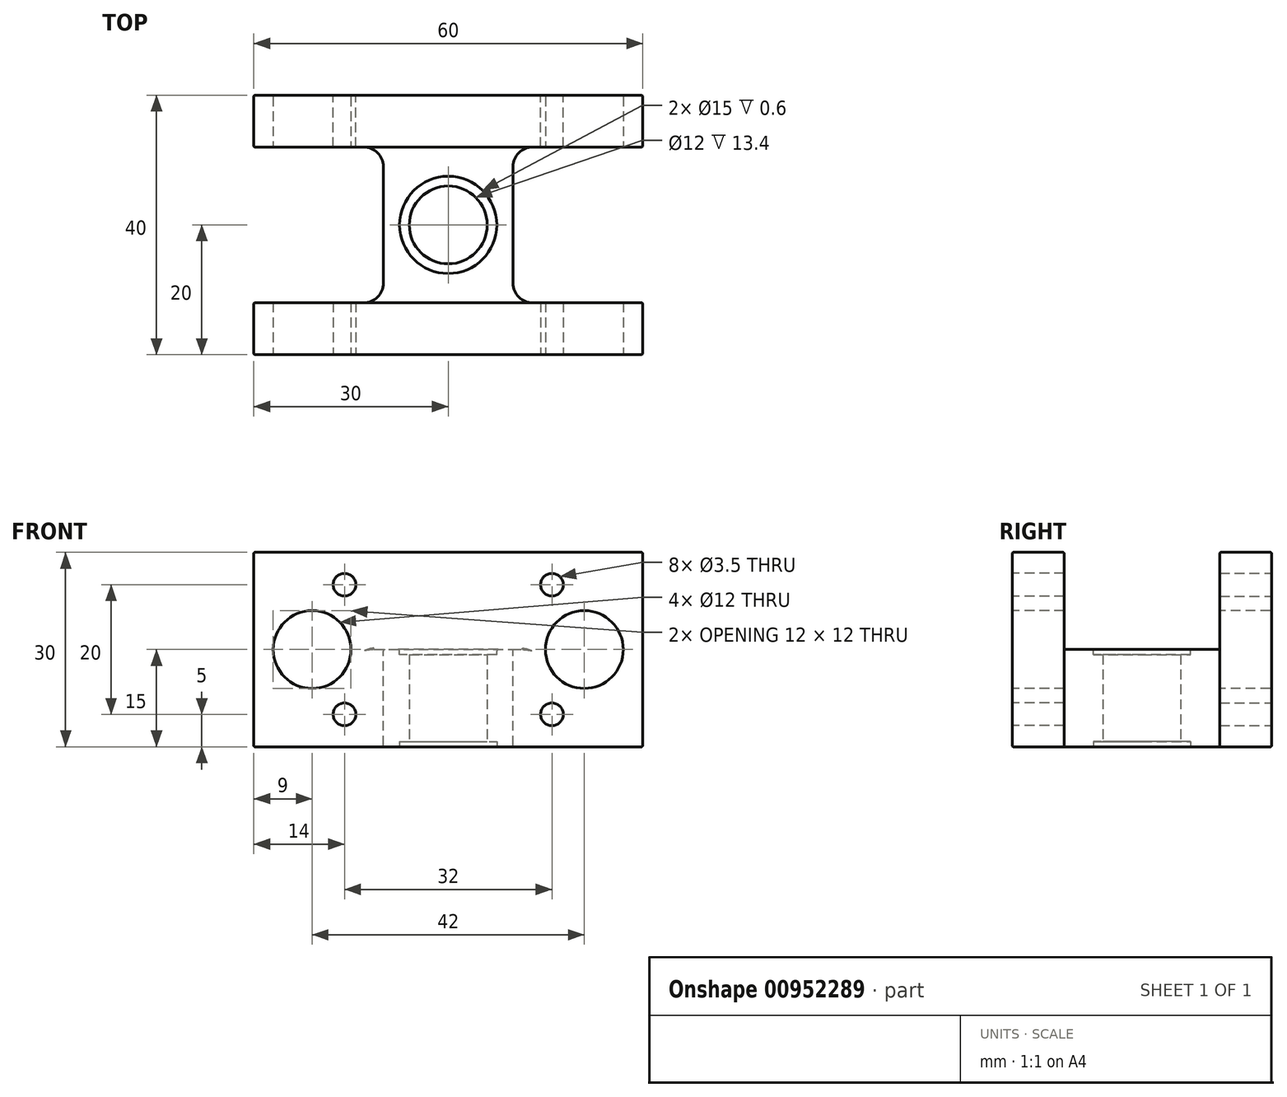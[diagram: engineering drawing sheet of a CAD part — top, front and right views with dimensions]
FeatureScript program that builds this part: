
annotation { "Feature Type Name" : "Feature", "Feature Type Description" : "" }
export const myFeature = defineFeature(function(context is Context, id is Id, definition is map)
    precondition{}
    {
        {
            var Q0;
            Q0=qCreatedBy(makeId("Top.planeOp"),FACE);
            var sketch = newSketch(context, id + "F0", { "sketchPlane" : qUnion([Q0])});
            skLineSegment(sketch, "E0.bottom", {"start": v(30, -20) * mm, "end": v(-30, -20) * mm});
            skLineSegment(sketch, "E0.top", {"start": v(30, 20) * mm, "end": v(-30, 20) * mm});
            skLineSegment(sketch, "E0.left", {"start": v(30, -20) * mm, "end": v(30, 20) * mm});
            skLineSegment(sketch, "E0.right", {"start": v(-30, -20) * mm, "end": v(-30, 20) * mm});
            skPoint(sketch, "E0.middle", {"position": v(0, 0) * mm});
            skCircle(sketch, "E1", {"center": v(0, 0) * mm, "radius": 6 * mm});
            skSolve(sketch);
        }
        {
            var Q0;
            Q0 = qSketchRegion(id + "F0", true);
            extrude(context, id + "F1", {"entities" : qUnion([Q0]), "depth" : 15 * mm, "offsetDistance" : 25 * mm, "symmetric" : true});
        }
        {
            var Q0;
            Q0=makeQuery(id+"F1.opExtrude","SWEPT_FACE",FACE,{"disambiguationData":[OSD([sQuery(id+"F0.wireOp",EDGE,"E0.left")])]});
            var sketch = newSketch(context, id + "F2", { "sketchPlane" : qUnion([Q0])});
            skLineSegment(sketch, "E2.bottom", {"start": v(20, 7.5) * mm, "end": v(12, 7.5) * mm});
            skLineSegment(sketch, "E2.top", {"start": v(20, 22.5) * mm, "end": v(12, 22.5) * mm});
            skLineSegment(sketch, "E2.left", {"start": v(20, 7.5) * mm, "end": v(20, 22.5) * mm});
            skLineSegment(sketch, "E2.right", {"start": v(12, 7.5) * mm, "end": v(12, 22.5) * mm});
            skLineSegment(sketch, "E3.MirrorCS", {"start": v(-12, 7.5) * mm, "end": v(-12, 22.5) * mm});
            skLineSegment(sketch, "E4.MirrorCS", {"start": v(-20, 22.5) * mm, "end": v(-12, 22.5) * mm});
            skLineSegment(sketch, "E5.MirrorCS", {"start": v(-20, 7.5) * mm, "end": v(-20, 22.5) * mm});
            skSolve(sketch);
        }
        {
            var Q0;
            Q0 = qSketchRegion(id + "F2", true);
            var Q1;
            {var subQ0=sQuery(id+"F2.wireOp",EDGE,"E3.MirrorCS");Q1=makeQuery(id+"F2.imprint","IMPRINT",FACE,{"disambiguationData":[TD([[makeQuery(id+"F2.imprint","IMPRINT",EDGE,{"derivedFrom":subQ0}),1.0]])]});}
            var Q2;
            Q2=makeQuery(id+"F1.opExtrude","SWEPT_FACE",FACE,{"disambiguationData":[OSD([sQuery(id+"F0.wireOp",EDGE,"E0.right")])]});
            extrude(context, id + "F3", {"entities" : qUnion([Q0, Q1]), "operationType" : NewBodyOperationType.ADD, "endBound" : BoundingType.UP_TO_SURFACE, "oppositeDirection" : true, "depth" : 25 * mm, "endBoundEntityFace" : qUnion([Q2]), "offsetDistance" : 25 * mm});
        }
        {
            var Q0;
            Q0=makeQuery(id+"F3.boolean.opBoolean","MERGE",FACE,{"derivedFrom":[makeQuery(id+"F1.opExtrude","SWEPT_FACE",FACE,{"disambiguationData":[OSD([sQuery(id+"F0.wireOp",EDGE,"E0.top")])]}),makeQuery(id+"F3.opExtrude","SWEPT_FACE",FACE,{"disambiguationData":[OSD([sQuery(id+"F2.wireOp",EDGE,"E2.left")])]})]});
            var sketch = newSketch(context, id + "F4", { "sketchPlane" : qUnion([Q0])});
            skCircle(sketch, "E6", {"center": v(16, 17.5) * mm, "radius": 1.75 * mm});
            skCircle(sketch, "E7.MirrorC", {"center": v(-16, 17.5) * mm, "radius": 1.75 * mm});
            skLineSegment(sketch, "E8", {"start": v(30, 7.5) * mm, "end": v(17.34, 7.5) * mm});
            skCircle(sketch, "E9.MirrorC", {"center": v(16, -2.5) * mm, "radius": 1.75 * mm});
            skCircle(sketch, "E10.MirrorC", {"center": v(-16, -2.5) * mm, "radius": 1.75 * mm});
            skSolve(sketch);
        }
        {
            var Q0;
            Q0 = qSketchRegion(id + "F4", true);
            var Q1;
            Q1=makeQuery(id+"F3.opExtrude","SWEPT_FACE",FACE,{"disambiguationData":[OSD([sQuery(id+"F2.wireOp",EDGE,"E2.right")])]});
            extrude(context, id + "F5", {"entities" : qUnion([Q0]), "operationType" : NewBodyOperationType.REMOVE, "oppositeDirection" : true, "depth" : 8 * mm, "endBoundEntityFace" : qUnion([Q1]), "offsetDistance" : 25 * mm});
        }
        {
            var Q0;
            Q0=makeQuery(id+"F3.boolean.opBoolean","MERGE",FACE,{"derivedFrom":[makeQuery(id+"F1.opExtrude","SWEPT_FACE",FACE,{"disambiguationData":[OSD([sQuery(id+"F0.wireOp",EDGE,"E0.bottom")])]}),makeQuery(id+"F3.opExtrude","SWEPT_FACE",FACE,{"disambiguationData":[OSD([sQuery(id+"F2.wireOp",EDGE,"E5.MirrorCS")])]})]});
            var sketch = newSketch(context, id + "F6", { "sketchPlane" : qUnion([Q0])});
            skCircle(sketch, "E11", {"center": v(16, 17.5) * mm, "radius": 1.75 * mm});
            skCircle(sketch, "E12.MirrorC", {"center": v(-16, 17.5) * mm, "radius": 1.75 * mm});
            skLineSegment(sketch, "E13", {"start": v(30, 7.5) * mm, "end": v(18.29, 7.5) * mm});
            skCircle(sketch, "E14.MirrorC", {"center": v(16, -2.5) * mm, "radius": 1.75 * mm});
            skCircle(sketch, "E15.MirrorC", {"center": v(-16, -2.5) * mm, "radius": 1.75 * mm});
            skSolve(sketch);
        }
        {
            var Q0;
            Q0 = qSketchRegion(id + "F6", true);
            var Q1;
            Q1=makeQuery(id+"F3.opExtrude","SWEPT_FACE",FACE,{"disambiguationData":[OSD([sQuery(id+"F2.wireOp",EDGE,"E3.MirrorCS")])]});
            extrude(context, id + "F7", {"entities" : qUnion([Q0]), "operationType" : NewBodyOperationType.REMOVE, "oppositeDirection" : true, "depth" : 8 * mm, "endBoundEntityFace" : qUnion([Q1]), "offsetDistance" : 25 * mm});
        }
        {
            var Q0;
            Q0=makeQuery(id+"F1.opExtrude","CAP_FACE",FACE,{"disambiguationData":[OSD([sQuery(id+"F0.wireOp",EDGE,"E0.bottom"),sQuery(id+"F0.wireOp",EDGE,"E0.top"),sQuery(id+"F0.wireOp",EDGE,"E0.left"),sQuery(id+"F0.wireOp",EDGE,"E0.right"),sQuery(id+"F0.wireOp",EDGE,"E1")])],"isStart":false});
            var sketch = newSketch(context, id + "F8", { "sketchPlane" : qUnion([Q0])});
            skCircle(sketch, "E16", {"center": v(0, 0) * mm, "radius": 7.5 * mm});
            skSolve(sketch);
        }
        {
            var Q0;
            Q0 = qSketchRegion(id + "F8", true);
            extrude(context, id + "F9", {"entities" : qUnion([Q0]), "operationType" : NewBodyOperationType.REMOVE, "oppositeDirection" : true, "depth" : 0.8 * mm, "offsetDistance" : 25 * mm});
        }
        {
            var Q0;
            Q0=makeQuery(id+"F1.opExtrude","CAP_FACE",FACE,{"disambiguationData":[OSD([sQuery(id+"F0.wireOp",EDGE,"E0.bottom"),sQuery(id+"F0.wireOp",EDGE,"E0.top"),sQuery(id+"F0.wireOp",EDGE,"E0.left"),sQuery(id+"F0.wireOp",EDGE,"E0.right"),sQuery(id+"F0.wireOp",EDGE,"E1")])],"isStart":true});
            var sketch = newSketch(context, id + "F10", { "sketchPlane" : qUnion([Q0])});
            skCircle(sketch, "E17", {"center": v(0, 0) * mm, "radius": 7.5 * mm});
            skSolve(sketch);
        }
        {
            var Q0;
            Q0 = qSketchRegion(id + "F10", true);
            extrude(context, id + "F11", {"entities" : qUnion([Q0]), "operationType" : NewBodyOperationType.REMOVE, "oppositeDirection" : true, "depth" : 0.8 * mm, "offsetDistance" : 25 * mm});
        }
        {
            var Q0;
            Q0=makeQuery(id+"F1.opExtrude","CAP_FACE",FACE,{"disambiguationData":[OSD([sQuery(id+"F0.wireOp",EDGE,"E0.bottom"),sQuery(id+"F0.wireOp",EDGE,"E0.top"),sQuery(id+"F0.wireOp",EDGE,"E0.left"),sQuery(id+"F0.wireOp",EDGE,"E0.right"),sQuery(id+"F0.wireOp",EDGE,"E1")])],"isStart":false});
            var sketch = newSketch(context, id + "F12", { "sketchPlane" : qUnion([Q0])});
            skLineSegment(sketch, "E18.bottom", {"start": v(10, 12) * mm, "end": v(30, 12) * mm});
            skLineSegment(sketch, "E18.top", {"start": v(10, -12) * mm, "end": v(30, -12) * mm});
            skLineSegment(sketch, "E18.left", {"start": v(10, 12) * mm, "end": v(10, -12) * mm});
            skLineSegment(sketch, "E18.right", {"start": v(30, 12) * mm, "end": v(30, -12) * mm});
            skLineSegment(sketch, "E19.MirrorCS", {"start": v(-10, 12) * mm, "end": v(-10, -12) * mm});
            skLineSegment(sketch, "E20.MirrorCS", {"start": v(-10, 12) * mm, "end": v(-30, 12) * mm});
            skLineSegment(sketch, "E21.MirrorCS", {"start": v(-10, -12) * mm, "end": v(-30, -12) * mm});
            skLineSegment(sketch, "E22.MirrorCS", {"start": v(-30, 12) * mm, "end": v(-30, -12) * mm});
            skSolve(sketch);
        }
        {
            var Q0;
            Q0 = qSketchRegion(id + "F12", true);
            extrude(context, id + "F13", {"entities" : qUnion([Q0]), "operationType" : NewBodyOperationType.REMOVE, "oppositeDirection" : true, "depth" : 25 * mm, "offsetDistance" : 25 * mm});
        }
        {
            var Q0;
            Q0=makeQuery(id+"F13.boolean.opBoolean","COPY",EDGE,{"derivedFrom":makeQuery(id+"F13.opExtrude","SWEPT_EDGE",EDGE,{"disambiguationData":[OSD([sQuery(id+"F0.wireOp",EDGE,"E0.left"),sQuery(id+"F2.wireOp",EDGE,"E2.bottom"),sQuery(id+"F2.wireOp",EDGE,"E2.right"),sQuery(id+"F12.wireOp",EDGE,"E19.MirrorCS"),sQuery(id+"F12.wireOp",EDGE,"E20.MirrorCS")])]})});
            var Q1;
            Q1=makeQuery(id+"F13.boolean.opBoolean","COPY",EDGE,{"derivedFrom":makeQuery(id+"F13.opExtrude","SWEPT_EDGE",EDGE,{"disambiguationData":[OSD([sQuery(id+"F0.wireOp",EDGE,"E0.left"),sQuery(id+"F2.wireOp",EDGE,"E3.MirrorCS"),sQuery(id+"F12.wireOp",EDGE,"E19.MirrorCS"),sQuery(id+"F12.wireOp",EDGE,"E21.MirrorCS")])]})});
            var Q2;
            Q2=makeQuery(id+"F13.boolean.opBoolean","COPY",EDGE,{"derivedFrom":makeQuery(id+"F13.opExtrude","SWEPT_EDGE",EDGE,{"disambiguationData":[OSD([sQuery(id+"F0.wireOp",EDGE,"E0.left"),sQuery(id+"F2.wireOp",EDGE,"E2.bottom"),sQuery(id+"F2.wireOp",EDGE,"E2.right"),sQuery(id+"F12.wireOp",EDGE,"E18.bottom"),sQuery(id+"F12.wireOp",EDGE,"E18.left")])]})});
            var Q3;
            Q3=makeQuery(id+"F13.boolean.opBoolean","COPY",EDGE,{"derivedFrom":makeQuery(id+"F13.opExtrude","SWEPT_EDGE",EDGE,{"disambiguationData":[OSD([sQuery(id+"F0.wireOp",EDGE,"E0.left"),sQuery(id+"F2.wireOp",EDGE,"E3.MirrorCS"),sQuery(id+"F12.wireOp",EDGE,"E18.top"),sQuery(id+"F12.wireOp",EDGE,"E18.left")])]})});
            fillet(context, id + "F14", {"entities" : qUnion([Q0, Q1, Q2, Q3]), "tangentPropagation" : true, "radius" : 3 * mm, "defaultsChanged" : true, "vertexSettings" : [], "allowEdgeOverflow" : false});
        }
        {
            var Q0;
            Q0=makeQuery(id+"F3.boolean.opBoolean","MERGE",FACE,{"derivedFrom":[makeQuery(id+"F1.opExtrude","SWEPT_FACE",FACE,{"disambiguationData":[OSD([sQuery(id+"F0.wireOp",EDGE,"E0.bottom")])]}),makeQuery(id+"F3.opExtrude","SWEPT_FACE",FACE,{"disambiguationData":[OSD([sQuery(id+"F2.wireOp",EDGE,"E5.MirrorCS")])]})]});
            var sketch = newSketch(context, id + "F15", { "sketchPlane" : qUnion([Q0])});
            skCircle(sketch, "E23", {"center": v(-21, 7.5) * mm, "radius": 6 * mm});
            skCircle(sketch, "E24.MirrorC", {"center": v(21, 7.5) * mm, "radius": 6 * mm});
            skSolve(sketch);
        }
        {
            var Q0;
            Q0 = qSketchRegion(id + "F15", true);
            extrude(context, id + "F16", {"entities" : qUnion([Q0]), "operationType" : NewBodyOperationType.REMOVE, "endBound" : BoundingType.THROUGH_ALL, "oppositeDirection" : true, "depth" : 25 * mm, "offsetDistance" : 25 * mm});
        }
        {
            var Q0;
            Q0=makeQuery(id+"F1.opExtrude","CAP_FACE",FACE,{"disambiguationData":[OSD([sQuery(id+"F0.wireOp",EDGE,"E0.bottom"),sQuery(id+"F0.wireOp",EDGE,"E0.top"),sQuery(id+"F0.wireOp",EDGE,"E0.left"),sQuery(id+"F0.wireOp",EDGE,"E0.right"),sQuery(id+"F0.wireOp",EDGE,"E1")])],"isStart":true});
            var Q1;
            Q1=makeQuery(id+"F3.boolean.opBoolean","MERGE",FACE,{"derivedFrom":[makeQuery(id+"F1.opExtrude","SWEPT_FACE",FACE,{"disambiguationData":[OSD([sQuery(id+"F0.wireOp",EDGE,"E0.bottom")])]}),makeQuery(id+"F3.opExtrude","SWEPT_FACE",FACE,{"disambiguationData":[OSD([sQuery(id+"F2.wireOp",EDGE,"E5.MirrorCS")])]})]});
            var Q2;
            Q2=makeQuery(id+"F3.boolean.opBoolean","MERGE",FACE,{"derivedFrom":[makeQuery(id+"F1.opExtrude","SWEPT_FACE",FACE,{"disambiguationData":[OSD([sQuery(id+"F0.wireOp",EDGE,"E0.top")])]}),makeQuery(id+"F3.opExtrude","SWEPT_FACE",FACE,{"disambiguationData":[OSD([sQuery(id+"F2.wireOp",EDGE,"E2.left")])]})]});
            var Q3;
            Q3=makeQuery(id+"F3.opExtrude","SWEPT_FACE",FACE,{"disambiguationData":[OSD([sQuery(id+"F2.wireOp",EDGE,"E2.top")])]});
            var Q4;
            Q4=makeQuery(id+"F3.opExtrude","SWEPT_FACE",FACE,{"disambiguationData":[OSD([sQuery(id+"F2.wireOp",EDGE,"E4.MirrorCS")])]});
            var Q5;
            Q5=makeQuery(id+"F3.boolean.opBoolean","MERGE",FACE,{"derivedFrom":[makeQuery(id+"F1.opExtrude","SWEPT_FACE",FACE,{"disambiguationData":[OSD([sQuery(id+"F0.wireOp",EDGE,"E0.right")])]}),makeQuery(id+"F3.opExtrude","CAP_FACE",FACE,{"disambiguationData":[OSD([sQuery(id+"F2.wireOp",EDGE,"E2.bottom"),sQuery(id+"F2.wireOp",EDGE,"E2.top"),sQuery(id+"F2.wireOp",EDGE,"E2.left"),sQuery(id+"F2.wireOp",EDGE,"E2.right")])],"isStart":false}),makeQuery(id+"F3.opExtrude","CAP_FACE",FACE,{"disambiguationData":[OSD([sQuery(id+"F0.wireOp",EDGE,"E0.left"),sQuery(id+"F2.wireOp",EDGE,"E3.MirrorCS"),sQuery(id+"F2.wireOp",EDGE,"E4.MirrorCS"),sQuery(id+"F2.wireOp",EDGE,"E5.MirrorCS")])],"isStart":false})]});
            var Q6;
            {var subQ0=sQuery(id+"F0.wireOp",EDGE,"E0.left");Q6=makeQuery(id+"F3.boolean.opBoolean","MERGE",FACE,{"derivedFrom":[makeQuery(id+"F1.opExtrude","SWEPT_FACE",FACE,{"disambiguationData":[OSD([subQ0])]}),makeQuery(id+"F3.opExtrude","CAP_FACE",FACE,{"disambiguationData":[OSD([sQuery(id+"F2.wireOp",EDGE,"E2.bottom"),sQuery(id+"F2.wireOp",EDGE,"E2.top"),sQuery(id+"F2.wireOp",EDGE,"E2.left"),sQuery(id+"F2.wireOp",EDGE,"E2.right")])],"isStart":true}),makeQuery(id+"F3.opExtrude","CAP_FACE",FACE,{"disambiguationData":[OSD([subQ0,sQuery(id+"F2.wireOp",EDGE,"E3.MirrorCS"),sQuery(id+"F2.wireOp",EDGE,"E4.MirrorCS"),sQuery(id+"F2.wireOp",EDGE,"E5.MirrorCS")])],"isStart":true})]});}
            var Q7;
            Q7=makeQuery(id+"F1.opExtrude","CAP_FACE",FACE,{"disambiguationData":[OSD([sQuery(id+"F0.wireOp",EDGE,"E0.bottom"),sQuery(id+"F0.wireOp",EDGE,"E0.top"),sQuery(id+"F0.wireOp",EDGE,"E0.left"),sQuery(id+"F0.wireOp",EDGE,"E0.right"),sQuery(id+"F0.wireOp",EDGE,"E1")])],"isStart":false});
            fillet(context, id + "F17", {"entities" : qUnion([Q0, Q1, Q2, Q3, Q4, Q5, Q6, Q7]), "tangentPropagation" : true, "radius" : 0.2 * mm, "defaultsChanged" : false, "vertexSettings" : [], "allowEdgeOverflow" : false});
        }
    });
